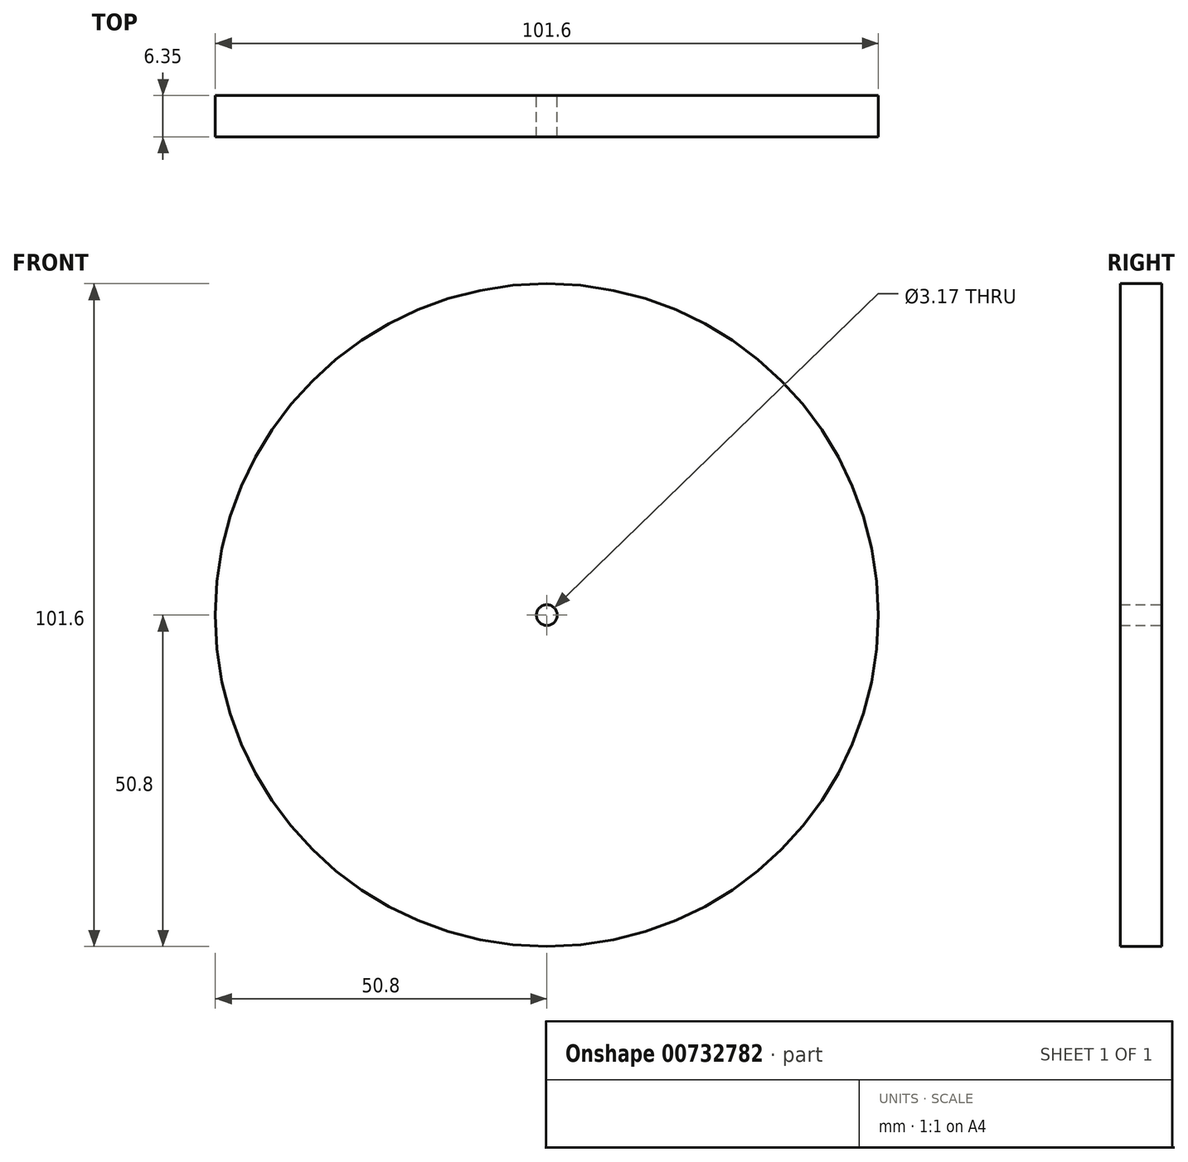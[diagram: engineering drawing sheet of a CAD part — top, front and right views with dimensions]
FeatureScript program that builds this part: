
annotation { "Feature Type Name" : "Feature", "Feature Type Description" : "" }
export const myFeature = defineFeature(function(context is Context, id is Id, definition is map)
    precondition{}
    {
        {
            var Q0;
            Q0=qCreatedBy(makeId("Front.planeOp"),FACE);
            var sketch = newSketch(context, id + "F0", { "sketchPlane" : qUnion([Q0])});
            skCircle(sketch, "E0", {"center": v(0, 0) * mm, "radius": 50.8 * mm});
            skCircle(sketch, "E1", {"center": v(0, 0) * mm, "radius": 1.59 * mm});
            skSolve(sketch);
        }
        {
            var Q0;
            Q0=makeQuery(id+"F0.imprint","IMPRINT",FACE,{"disambiguationData":[TD([[makeQuery(id+"F0.imprint","IMPRINT",EDGE,{"derivedFrom":sQuery(id+"F0.wireOp",EDGE,"E0")}),1.0]])]});
            extrude(context, id + "F1", {"entities" : qUnion([Q0]), "depth" : 6.35 * mm, "offsetDistance" : 25.4 * mm});
        }
    });
